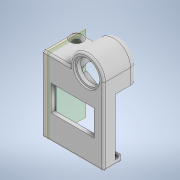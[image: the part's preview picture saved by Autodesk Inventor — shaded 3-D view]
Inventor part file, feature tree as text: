
AUTODESK INVENTOR PART (.ipt)
format: ipt  version: 2020.3 (Build 243373000, 373)  size: 442,880 bytes
history: native  units: mm
features: extrude x13, sketch x13, fillet x4, projected_geometry x3, plane x1, chamfer x1
ambient origin geometry x8: Origin, YZ Plane, XZ Plane, XY Plane, X Axis, Y Axis, Z Axis, Center Point
bodies: Volumenkörper1 (feature_tree)
feature tree (35):
  extrude  "Extrusion1"  Depth=11.2mm
  extrude  "Extrusion2"  Depth=13.4mm
  extrude  "Extrusion3"  Depth=6.0mm TaperAngle=0.0deg
  extrude  "Extrusion5"  Depth=17.6mm
  extrude  "Extrusion7"  Depth=1.5mm
  extrude  "Extrusion8"  Depth=1.5mm TaperAngle=0.0deg
  extrude  "Extrusion9"  Depth=4.5mm
  extrude  "Extrusion10"  Depth=6.0mm
  fillet  "Rundung3"  Radius=2.8mm
  fillet  "Rundung4"  Radius=2.0mm
  extrude  "Extrusion11"  Depth=10.0mm
  extrude  "Extrusion12"  Depth=36.0mm
  extrude  "Extrusion13"  Depth=12.7mm
  plane  "Arbeitsebene1"
  extrude  "Extrusion14"  Depth=16.2mm
  chamfer  "Fase1"  Distance=3.0mm
  extrude  "Extrusion16"  Depth=2.5mm
  fillet  "Rundung5"  Radius=13.8mm
  fillet  "Rundung6"  Radius=1.0mm
  sketch  "Skizze1"  dims[d0=22.4mm d1=11.2mm]
  sketch  "Skizze2"  dims[d2=30.4mm d3=16.0mm d4=13.4mm]
  sketch  "Skizze3"  dims[d5=6.7mm d9=6.0mm d10=0.0mm]
  sketch  "Skizze5"  dims[d11=25.4mm d12=17.6mm]
  sketch  "Skizze7"  dims[d15=4.0mm d16=0.0mm d19=1.5mm]
  sketch  "Skizze8"  dims[d20=1.5mm d21=2.2mm d22=0.0mm]
  projected_geometry  "Projizierte Kontur1"
  sketch  "Skizze9"  dims[d24=9.0mm d25=4.5mm]
  projected_geometry  "Projizierte Kontur2"
  sketch  "Skizze10"  dims[d26=12.0mm d27=6.0mm d28=2.8mm d29=2.0mm]
  projected_geometry  "Projizierte Kontur3"
  sketch  "Skizze11"  dims[d32=12.0mm d33=17.6mm d36=10.0mm d37=3.5mm]
  sketch  "Skizze12"  dims[d42=3.5mm d43=36.0mm]
  sketch  "Skizze13"  dims[d44=6.4mm d45=12.7mm]
  sketch  "Skizze14"  dims[d46=4.9mm d51=16.2mm d52=3.0mm d53=0.0mm]
  sketch  "Skizze16"  dims[d54=1.2mm d55=27.8mm d58=13.8mm d59=1.0mm d60=0.0mm d62=16.0mm d68=8.8mm d69=8.8mm d72=37.0mm d73=0.0mm d74=14.4mm d75=1.4mm d76=1.4mm d77=1.4mm d78=3.0mm d79=0.0mm d80=7.0mm d81=0.0mm d82=10.0mm d83=2.0mm d84=0.0mm d85=2.0mm d86=4.0mm d87=4.0mm d88=3.0mm d89=20.25mm d90=0.0mm d91=3.5mm d92=4.0mm d93=4.0mm d94=10.0mm d95=0.0mm d96=5.0mm d97=11.0mm d98=10.0mm d99=0.0mm d100=-4.0mm d101=1.9mm d102=0.5mm d103=0.0mm d104=1.5mm d105=2.0mm d106=45.0deg d111=3.0mm d112=2.8mm d113=1.6mm d114=0.6mm d115=10.0mm d116=0.0mm d117=1.0mm d118=2.5mm d119=0.4mm]
